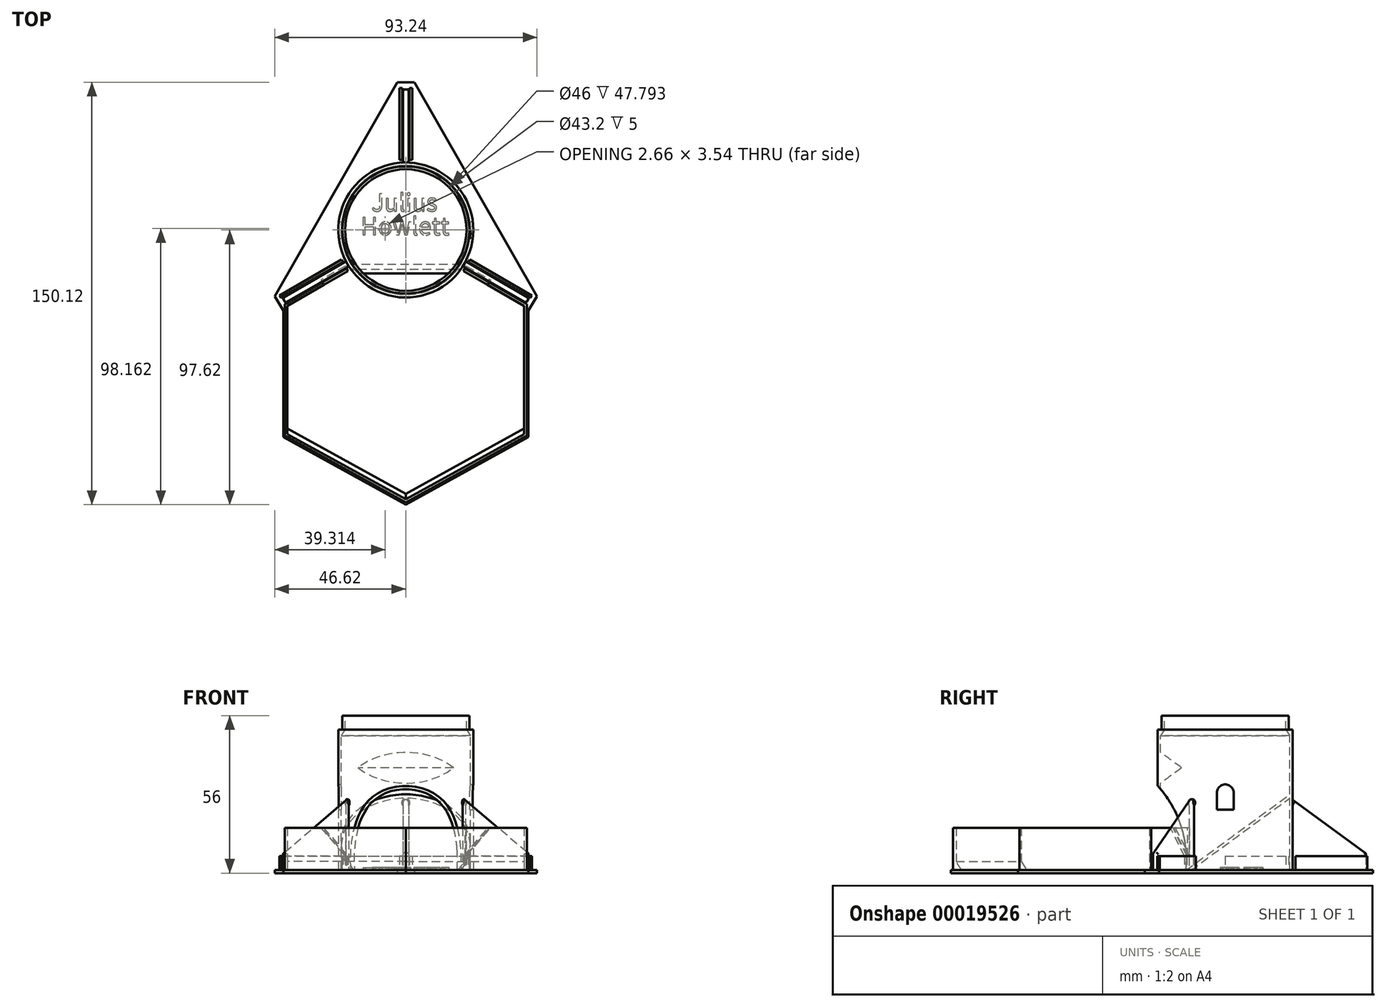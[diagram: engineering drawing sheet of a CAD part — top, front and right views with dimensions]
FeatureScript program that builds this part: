
annotation { "Feature Type Name" : "Feature", "Feature Type Description" : "" }
export const myFeature = defineFeature(function(context is Context, id is Id, definition is map)
    precondition{}
    {
        {
            var Q0;
            Q0=qCreatedBy(makeId("Top.planeOp"),FACE);
            var sketch = newSketch(context, id + "F0", { "sketchPlane" : qUnion([Q0])});
            skCircle(sketch, "E0", {"center": v(0, 0) * mm, "radius": 24 * mm});
            skSolve(sketch);
        }
        {
            var Q0;
            Q0=makeQuery(id+"F0.imprint","IMPRINT",FACE,{"disambiguationData":[TD([[makeQuery(id+"F0.imprint","IMPRINT",EDGE,{"derivedFrom":sQuery(id+"F0.wireOp",EDGE,"E0")}),1.0]])]});
            extrude(context, id + "F1", {"entities" : qUnion([Q0]), "depth" : 50 * mm});
        }
        {
            var Q0;
            Q0=makeQuery(id+"F1.opExtrude","CAP_FACE",FACE,{"disambiguationData":[OSD([sQuery(id+"F0.wireOp",EDGE,"E0")])],"isStart":false});
            var sketch = newSketch(context, id + "F2", { "sketchPlane" : qUnion([Q0])});
            skCircle(sketch, "E1", {"center": v(0, 0) * mm, "radius": 23 * mm});
            skSolve(sketch);
        }
        {
            var Q0;
            Q0=qSketchRegion(id+"F2",true);
            extrude(context, id + "F3", {"entities" : qUnion([Q0]), "operationType" : NewBodyOperationType.REMOVE, "endBound" : BoundingType.THROUGH_ALL, "oppositeDirection" : true, "depth" : 25 * mm});
        }
        {
            var Q0;
            Q0=qCreatedBy(makeId("Front.planeOp"),FACE);
            var sketch = newSketch(context, id + "F4", { "sketchPlane" : qUnion([Q0])});
            skLineSegment(sketch, "E2", {"start": v(0, 0) * mm, "end": v(0, 50) * mm});
            skLineSegment(sketch, "E3.0", {"start": v(-23.5, 50) * mm, "end": v(-23.5, 47) * mm});
            skLineSegment(sketch, "E4", {"start": v(-23.5, 50) * mm, "end": v(-22.6, 50) * mm});
            skLineSegment(sketch, "E5", {"start": v(-22.6, 50) * mm, "end": v(-22.6, 55) * mm});
            skLineSegment(sketch, "E6", {"start": v(-22.6, 55) * mm, "end": v(-21.6, 55) * mm});
            skLineSegment(sketch, "E7", {"start": v(-21.6, 55) * mm, "end": v(-21.6, 50) * mm});
            skLineSegment(sketch, "E8", {"start": v(-21.6, 50) * mm, "end": v(-23.5, 47) * mm});
            skLineSegment(sketch, "E9", {"start": v(-24, 50) * mm, "end": v(-23.5, 50) * mm});
            skSolve(sketch);
        }
        {
            var Q0;
            Q0=qSketchRegion(id+"F4",true);
            var Q1;
            Q1=makeQuery(id+"F3.boolean.opBoolean","COPY",FACE,{"derivedFrom":makeQuery(id+"F3.opExtrude","SWEPT_FACE",FACE,{"disambiguationData":[OSD([sQuery(id+"F2.wireOp",EDGE,"E1")])]})});
            revolve(context, id + "F5", {"operationType" : NewBodyOperationType.ADD, "entities" : qUnion([Q0]), "axis" : qUnion([Q1]), "revolveType" : RevolveType.FULL});
        }
        {
            var Q0;
            Q0=qCreatedBy(makeId("Top.planeOp"),FACE);
            var sketch = newSketch(context, id + "F6", { "sketchPlane" : qUnion([Q0])});
            skLineSegment(sketch, "E10", {"start": v(-1, 50) * mm, "end": v(-1, 23.5) * mm});
            skLineSegment(sketch, "E11", {"start": v(-1, 23.5) * mm, "end": v(1, 23.5) * mm});
            skLineSegment(sketch, "E12", {"start": v(1, 23.5) * mm, "end": v(1, 50) * mm});
            skLineSegment(sketch, "E13", {"start": v(-1, 50) * mm, "end": v(1, 50) * mm});
            skLineSegment(sketch, "E14.1.4", {"start": v(-20.85, -10.88) * mm, "end": v(-43.8, -24.13) * mm});
            skLineSegment(sketch, "E14.1.6", {"start": v(-42.8, -25.87) * mm, "end": v(-19.85, -12.62) * mm});
            skLineSegment(sketch, "E14.1.8", {"start": v(-19.85, -12.62) * mm, "end": v(-20.85, -10.88) * mm});
            skLineSegment(sketch, "E14.1.11", {"start": v(-42.8, -25.87) * mm, "end": v(-43.8, -24.13) * mm});
            skLineSegment(sketch, "E14.2.4", {"start": v(19.85, -12.62) * mm, "end": v(42.8, -25.87) * mm});
            skLineSegment(sketch, "E14.2.6", {"start": v(43.8, -24.13) * mm, "end": v(20.85, -10.88) * mm});
            skLineSegment(sketch, "E14.2.8", {"start": v(20.85, -10.88) * mm, "end": v(19.85, -12.62) * mm});
            skLineSegment(sketch, "E14.2.11", {"start": v(43.8, -24.13) * mm, "end": v(42.8, -25.87) * mm});
            skPoint(sketch, "E14.center", {"position": v(0, 0) * mm});
            skLineSegment(sketch, "E15", {"start": v(0, 0) * mm, "end": v(-23, 0) * mm});
            skSolve(sketch);
        }
        {
            var Q0;
            Q0=qSketchRegion(id+"F6",true);
            extrude(context, id + "F7", {"entities" : qUnion([Q0]), "operationType" : NewBodyOperationType.ADD, "depth" : 25 * mm});
        }
        {
            var Q0;
            Q0=makeQuery(id+"F7.opExtrude","SWEPT_FACE",FACE,{"disambiguationData":[OSD([sQuery(id+"F6.wireOp",EDGE,"E14.1.6")])]});
            var sketch = newSketch(context, id + "F8", { "sketchPlane" : qUnion([Q0])});
            skLineSegment(sketch, "E16", {"start": v(-23.98, 25) * mm, "end": v(-50, 25) * mm});
            skLineSegment(sketch, "E17", {"start": v(-50, 25) * mm, "end": v(-50, 6) * mm});
            skLineSegment(sketch, "E18", {"start": v(-50, 6) * mm, "end": v(-23.98, 25) * mm});
            skSolve(sketch);
        }
        {
            var Q0;
            Q0=qSketchRegion(id+"F8",true);
            extrude(context, id + "F9", {"entities" : qUnion([Q0]), "operationType" : NewBodyOperationType.REMOVE, "oppositeDirection" : true, "depth" : 2 * mm});
        }
        {
            var Q0;
            Q0=makeQuery(id+"F7.opExtrude","SWEPT_FACE",FACE,{"disambiguationData":[OSD([sQuery(id+"F6.wireOp",EDGE,"E14.2.6")])]});
            var sketch = newSketch(context, id + "F10", { "sketchPlane" : qUnion([Q0])});
            skLineSegment(sketch, "E19", {"start": v(-23.98, 25) * mm, "end": v(-50, 25) * mm});
            skLineSegment(sketch, "E20", {"start": v(-50, 25) * mm, "end": v(-50, 6) * mm});
            skLineSegment(sketch, "E21", {"start": v(-50, 6) * mm, "end": v(-23.98, 25) * mm});
            skSolve(sketch);
        }
        {
            var Q0;
            Q0=qSketchRegion(id+"F10",true);
            extrude(context, id + "F11", {"entities" : qUnion([Q0]), "operationType" : NewBodyOperationType.REMOVE, "oppositeDirection" : true, "depth" : 2 * mm});
        }
        {
            var Q0;
            Q0=makeQuery(id+"F7.opExtrude","SWEPT_FACE",FACE,{"disambiguationData":[OSD([sQuery(id+"F6.wireOp",EDGE,"E10")])]});
            var sketch = newSketch(context, id + "F12", { "sketchPlane" : qUnion([Q0])});
            skLineSegment(sketch, "E22", {"start": v(-23.98, 25) * mm, "end": v(-50, 25) * mm});
            skLineSegment(sketch, "E23", {"start": v(-50, 25) * mm, "end": v(-50, 6) * mm});
            skLineSegment(sketch, "E24", {"start": v(-23.98, 25) * mm, "end": v(-50, 6) * mm});
            skSolve(sketch);
        }
        {
            var Q0;
            Q0=qSketchRegion(id+"F12",true);
            extrude(context, id + "F13", {"entities" : qUnion([Q0]), "operationType" : NewBodyOperationType.REMOVE, "oppositeDirection" : true, "depth" : 2 * mm});
        }
        {
            var Q0;
            Q0=makeQuery(id+"F13.boolean.opBoolean","COPY",FACE,{"derivedFrom":makeQuery(id+"F13.opExtrude","SWEPT_FACE",FACE,{"disambiguationData":[OSD([sQuery(id+"F12.wireOp",EDGE,"E24")])]})});
            var Q1;
            Q1=makeQuery(id+"F9.boolean.opBoolean","COPY",FACE,{"derivedFrom":makeQuery(id+"F9.opExtrude","SWEPT_FACE",FACE,{"disambiguationData":[OSD([sQuery(id+"F8.wireOp",EDGE,"E18")])]})});
            var Q2;
            Q2=makeQuery(id+"F11.boolean.opBoolean","COPY",FACE,{"derivedFrom":makeQuery(id+"F11.opExtrude","SWEPT_FACE",FACE,{"disambiguationData":[OSD([sQuery(id+"F10.wireOp",EDGE,"E21")])]})});
            fillet(context, id + "F14", {"entities" : qUnion([Q0, Q1, Q2]), "radius" : .5 * mm, "allowEdgeOverflow" : false});
        }
        {
            var Q0;
            Q0=makeQuery(id+"F7.opExtrude","SWEPT_FACE",FACE,{"disambiguationData":[OSD([sQuery(id+"F6.wireOp",EDGE,"E14.1.11")])]});
            var Q1;
            Q1=makeQuery(id+"F7.opExtrude","SWEPT_FACE",FACE,{"disambiguationData":[OSD([sQuery(id+"F6.wireOp",EDGE,"E14.2.11")])]});
            var Q2;
            Q2=makeQuery(id+"F7.opExtrude","SWEPT_FACE",FACE,{"disambiguationData":[OSD([sQuery(id+"F6.wireOp",EDGE,"E13")])]});
            fillet(context, id + "F15", {"entities" : qUnion([Q0, Q1, Q2]), "radius" : .5 * mm, "tangentPropagation" : true, "allowEdgeOverflow" : false});
        }
        {
            var Q0;
            Q0=qCreatedBy(makeId("Right.planeOp"),FACE);
            var sketch = newSketch(context, id + "F16", { "sketchPlane" : qUnion([Q0])});
            skLineSegment(sketch, "E25", {"start": v(-24, 0) * mm, "end": v(-24, 30) * mm});
            skArc(sketch, "E26", {"start": v(-14, 0) * mm, "mid": v(-15.84, 16.05) * mm, "end": v(-24, 30) * mm});
            skLineSegment(sketch, "E27", {"start": v(-24, 0) * mm, "end": v(-14, 0) * mm});
            skSolve(sketch);
        }
        {
            var Q0;
            Q0=qSketchRegion(id+"F16",true);
            extrude(context, id + "F17", {"entities" : qUnion([Q0]), "operationType" : NewBodyOperationType.REMOVE, "oppositeDirection" : true, "depth" : 20 * mm, "hasSecondDirection" : true, "secondDirectionOppositeDirection" : false, "secondDirectionDepth" : 20 * mm});
        }
        {
            var Q0;
            Q0=qCreatedBy(makeId("Right.planeOp"),FACE);
            var sketch = newSketch(context, id + "F18", { "sketchPlane" : qUnion([Q0])});
            skCircle(sketch, "E28", {"center": v(0, 27.55) * mm, "radius": 3 * mm});
            skLineSegment(sketch, "E29.rect.bottom", {"start": v(-3, 21.55) * mm, "end": v(3, 21.55) * mm});
            skLineSegment(sketch, "E29.rect.top", {"start": v(-3, 27.55) * mm, "end": v(3, 27.55) * mm});
            skLineSegment(sketch, "E29.rect.left", {"start": v(-3, 21.55) * mm, "end": v(-3, 27.55) * mm});
            skLineSegment(sketch, "E29.rect.right", {"start": v(3, 21.55) * mm, "end": v(3, 27.55) * mm});
            skPoint(sketch, "E29.rect.middle", {"position": v(0, 24.55) * mm});
            skSolve(sketch);
        }
        {
            var Q0;
            Q0=qSketchRegion(id+"F18",true);
            extrude(context, id + "F19", {"entities" : qUnion([Q0]), "operationType" : NewBodyOperationType.REMOVE, "endBound" : BoundingType.THROUGH_ALL, "oppositeDirection" : true, "depth" : 25 * mm, "hasSecondDirection" : true, "secondDirectionBound" : SecondDirectionBoundingType.THROUGH_ALL, "secondDirectionOppositeDirection" : false, "secondDirectionDepth" : 25 * mm});
        }
        {
            var Q0;
            Q0=qCreatedBy(makeId("Right.planeOp"),FACE);
            var sketch = newSketch(context, id + "F20", { "sketchPlane" : qUnion([Q0])});
            skPoint(sketch, "E30.0", {"position": v(-14, 0) * mm});
            skLineSegment(sketch, "E31", {"start": v(-12.2, 0) * mm, "end": v(-14, 0) * mm});
            skLineSegment(sketch, "E32", {"start": v(-14, 0) * mm, "end": v(23, 27) * mm});
            skLineSegment(sketch, "E33", {"start": v(-12.2, 0) * mm, "end": v(23, 25.7) * mm});
            skLineSegment(sketch, "E34", {"start": v(23, 27) * mm, "end": v(23, 25.7) * mm});
            skLineSegment(sketch, "E35", {"start": v(-23, 30.97) * mm, "end": v(-15.49, 36.45) * mm});
            skLineSegment(sketch, "E36", {"start": v(-15.49, 36.45) * mm, "end": v(-23, 41.91) * mm});
            skLineSegment(sketch, "E37", {"start": v(-23, 41.91) * mm, "end": v(-23, 30.97) * mm});
            skSolve(sketch);
        }
        {
            var Q0;
            Q0=qSketchRegion(id+"F20",true);
            extrude(context, id + "F21", {"entities" : qUnion([Q0]), "operationType" : NewBodyOperationType.ADD, "endBound" : BoundingType.UP_TO_NEXT, "depth" : 25 * mm, "hasSecondDirection" : true, "secondDirectionBound" : SecondDirectionBoundingType.UP_TO_NEXT, "secondDirectionOppositeDirection" : true, "secondDirectionDepth" : 25 * mm});
        }
        {
            var Q0;
            Q0=qCreatedBy(makeId("Right.planeOp"),FACE);
            var sketch = newSketch(context, id + "F22", { "sketchPlane" : qUnion([Q0])});
            skLineSegment(sketch, "E38", {"start": v(0, 0) * mm, "end": v(22.6, 0) * mm});
            skLineSegment(sketch, "E39", {"start": v(22.6, 0) * mm, "end": v(22.6, 5) * mm});
            skLineSegment(sketch, "E40", {"start": v(22.6, 5) * mm, "end": v(21.6, 5) * mm});
            skLineSegment(sketch, "E41", {"start": v(21.6, 5) * mm, "end": v(21.6, 0) * mm});
            skLineSegment(sketch, "E42", {"start": v(0, 0) * mm, "end": v(0, 8.05) * mm});
            skLineSegment(sketch, "E43", {"start": v(22.6, 0) * mm, "end": v(24.4, 0) * mm});
            skLineSegment(sketch, "E44", {"start": v(24.4, 5) * mm, "end": v(25.4, 5) * mm});
            skLineSegment(sketch, "E45", {"start": v(25.4, 5) * mm, "end": v(25.4, 0) * mm});
            skLineSegment(sketch, "E46", {"start": v(25.4, 0) * mm, "end": v(24.4, 0) * mm});
            skSolve(sketch);
        }
        {
            var Q0;
            Q0 = qSketchRegion(id + "F22", true);
            var Q1;
            Q1=sQuery(id+"F22.wireOp",EDGE,"E42");
            revolve(context, id + "F23", {"operationType" : NewBodyOperationType.ADD, "entities" : qUnion([Q0]), "axis" : qUnion([Q1]), "revolveType" : RevolveType.SYMMETRIC, "angle" : 180 * degree});
        }
        {
            var Q0;
            Q0=qCreatedBy(makeId("Top.planeOp"),FACE);
            var sketch = newSketch(context, id + "F24", { "sketchPlane" : qUnion([Q0])});
            skText(sketch, "E47", { "text": "  Julius\nHowlett", "fontName": "NotoSansCJKjp-Regular.otf"});
            const initialGuessF24  = {"E47": [-0.01603, 0.0067, 1, 0, 0.00609]};
            skSetInitialGuess(sketch, initialGuessF24);
            skSolve(sketch);
        }
        {
            var Q0;
            Q0 = qSketchRegion(id + "F24", true);
            extrude(context, id + "F25", {"entities" : qUnion([Q0]), "operationType" : NewBodyOperationType.ADD, "depth" : 1 * mm});
        }
        {
            var Q0;
            Q0=qCreatedBy(makeId("Top.planeOp"),FACE);
            var sketch = newSketch(context, id + "F26", { "sketchPlane" : qUnion([Q0])});
            skLineSegment(sketch, "E48.MirrorCS", {"start": v(1.3, 50.5) * mm, "end": v(1.3, 25) * mm});
            skLineSegment(sketch, "E49.MirrorCS", {"start": v(1.3, 25) * mm, "end": v(2.3, 25) * mm});
            skPoint(sketch, "E50.center", {"position": v(0, 0) * mm});
            skLineSegment(sketch, "E51", {"start": v(2.3, 25) * mm, "end": v(2.3, 50.5) * mm});
            skLineSegment(sketch, "E52", {"start": v(1.3, 50.5) * mm, "end": v(2.3, 50.5) * mm});
            skLineSegment(sketch, "E53", {"start": v(0, 25) * mm, "end": v(0, 0) * mm});
            skLineSegment(sketch, "E54.MirrorCS", {"start": v(-1.3, 50.5) * mm, "end": v(-1.3, 25) * mm});
            skLineSegment(sketch, "E55.MirrorCS", {"start": v(-1.3, 25) * mm, "end": v(-2.3, 25) * mm});
            skLineSegment(sketch, "E56.MirrorCS", {"start": v(-2.3, 25) * mm, "end": v(-2.3, 50.5) * mm});
            skLineSegment(sketch, "E57.MirrorCS", {"start": v(-1.3, 50.5) * mm, "end": v(-2.3, 50.5) * mm});
            skLineSegment(sketch, "E58.1.0", {"start": v(-43.08, -26.38) * mm, "end": v(-21, -13.63) * mm});
            skLineSegment(sketch, "E58.1.1", {"start": v(-44.38, -24.12) * mm, "end": v(-22.3, -11.37) * mm});
            skLineSegment(sketch, "E58.1.2", {"start": v(-22.8, -10.5) * mm, "end": v(-44.88, -23.26) * mm});
            skLineSegment(sketch, "E58.1.3", {"start": v(-20.5, -14.5) * mm, "end": v(-42.58, -27.24) * mm});
            skLineSegment(sketch, "E58.1.4", {"start": v(-21, -13.63) * mm, "end": v(-20.5, -14.5) * mm});
            skLineSegment(sketch, "E58.1.5", {"start": v(-22.3, -11.37) * mm, "end": v(-22.8, -10.5) * mm});
            skLineSegment(sketch, "E58.1.6", {"start": v(-43.08, -26.38) * mm, "end": v(-42.58, -27.24) * mm});
            skLineSegment(sketch, "E58.1.7", {"start": v(-44.38, -24.12) * mm, "end": v(-44.88, -23.26) * mm});
            skLineSegment(sketch, "E58.2.0", {"start": v(44.38, -24.12) * mm, "end": v(22.3, -11.37) * mm});
            skLineSegment(sketch, "E58.2.1", {"start": v(43.08, -26.38) * mm, "end": v(21, -13.63) * mm});
            skLineSegment(sketch, "E58.2.2", {"start": v(20.5, -14.5) * mm, "end": v(42.58, -27.24) * mm});
            skLineSegment(sketch, "E58.2.3", {"start": v(22.8, -10.5) * mm, "end": v(44.88, -23.26) * mm});
            skLineSegment(sketch, "E58.2.4", {"start": v(22.3, -11.37) * mm, "end": v(22.8, -10.5) * mm});
            skLineSegment(sketch, "E58.2.5", {"start": v(21, -13.63) * mm, "end": v(20.5, -14.5) * mm});
            skLineSegment(sketch, "E58.2.6", {"start": v(44.38, -24.12) * mm, "end": v(44.88, -23.26) * mm});
            skLineSegment(sketch, "E58.2.7", {"start": v(43.08, -26.38) * mm, "end": v(42.58, -27.24) * mm});
            skSolve(sketch);
        }
        {
            var Q0;
            Q0 = qSketchRegion(id + "F26", true);
            extrude(context, id + "F27", {"entities" : qUnion([Q0]), "operationType" : NewBodyOperationType.ADD, "depth" : 5 * mm});
        }
        {
            var Q0;
            Q0=qCreatedBy(makeId("Top.planeOp"),FACE);
            var sketch = newSketch(context, id + "F28", { "sketchPlane" : qUnion([Q0])});
            skLineSegment(sketch, "E59", {"start": v(0, 52.5) * mm, "end": v(-3.04, 52.5) * mm});
            skLineSegment(sketch, "E60", {"start": v(-3.04, 52.5) * mm, "end": v(-46.62, -23.51) * mm});
            skLineSegment(sketch, "E61.MirrorCS", {"start": v(3.04, 52.5) * mm, "end": v(46.62, -23.51) * mm});
            skLineSegment(sketch, "E62.MirrorCS", {"start": v(0, 52.5) * mm, "end": v(3.04, 52.5) * mm});
            skLineSegment(sketch, "E63", {"start": v(0, 0) * mm, "end": v(0, -52.5) * mm});
            skLineSegment(sketch, "E64", {"start": v(0, 0) * mm, "end": v(0, 52.5) * mm});
            skLineSegment(sketch, "E65", {"start": v(-46.62, -23.51) * mm, "end": v(-43.55, -28.67) * mm});
            skLineSegment(sketch, "E66.MirrorCS", {"start": v(46.62, -23.51) * mm, "end": v(43.55, -28.67) * mm});
            skLineSegment(sketch, "E67", {"start": v(-43.55, -28.67) * mm, "end": v(-43.55, -73.67) * mm});
            skLineSegment(sketch, "E68.MirrorCS", {"start": v(43.55, -28.67) * mm, "end": v(43.55, -73.67) * mm});
            skLineSegment(sketch, "E69", {"start": v(-43.55, -73.67) * mm, "end": v(0, -97.62) * mm});
            skLineSegment(sketch, "E70", {"start": v(0, -97.62) * mm, "end": v(43.55, -73.67) * mm});
            skSolve(sketch);
        }
        {
            var Q0;
            Q0 = qSketchRegion(id + "F28", true);
            extrude(context, id + "F29", {"entities" : qUnion([Q0]), "depth" : .1 * mm, "hasSecondDirection" : true, "secondDirectionOppositeDirection" : true, "secondDirectionDepth" : 1 * mm});
        }
        {
            var Q0;
            Q0=makeQuery(id+"F29.opExtrude","CAP_FACE",FACE,{"disambiguationData":[OSD([sQuery(id+"F28.wireOp",EDGE,"E59"),sQuery(id+"F28.wireOp",EDGE,"E60"),sQuery(id+"F28.wireOp",EDGE,"c55cebbd-51ed-417a-9139-d7e1a8fbc767"),sQuery(id+"F28.wireOp",EDGE,"2517fbf9-24b9-4a16-a406-ebb001d36d89"),sQuery(id+"F28.wireOp",EDGE,"b6296028-9263-4a43-9658-82991aeefb18"),sQuery(id+"F28.wireOp",EDGE,"9eefc208-e5e9-4d7a-b0e8-83d086b65d660.MirrorCS"),sQuery(id+"F28.wireOp",EDGE,"e3a6379c-8aaa-4815-999c-e2b0ab7a97050.MirrorCS"),sQuery(id+"F28.wireOp",EDGE,"34469dab-9091-40de-b46f-d139c8e73abb0.MirrorCS"),sQuery(id+"F28.wireOp",EDGE,"E61.MirrorCS"),sQuery(id+"F28.wireOp",EDGE,"E62.MirrorCS")])],"isStart":false});
            var sketch = newSketch(context, id + "F30", { "sketchPlane" : qUnion([Q0])});
            skSolve(sketch);
        }
        {
            var Q0;
            Q0=makeQuery(id+"F30.imprint","IMPRINT",FACE,{"disambiguationData":[TD([[makeQuery(id+"F30.imprint","IMPRINT",EDGE,{"derivedFrom":makeQuery(id+"F29.opExtrude","CAP_EDGE",EDGE,{"disambiguationData":[OSD([sQuery(id+"F28.wireOp",EDGE,"E60")])],"isStart":false})}),1.0]])]});
            var sketch = newSketch(context, id + "F31", { "sketchPlane" : qUnion([Q0])});
            skPoint(sketch, "E71.0", {"position": v(-21, -13.63) * mm});
            skPoint(sketch, "E72.0", {"position": v(-43.08, -26.38) * mm});
            skPoint(sketch, "E73.0", {"position": v(-20.5, -14.5) * mm});
            skLineSegment(sketch, "E74", {"start": v(-20.5, -14.5) * mm, "end": v(-21, -13.63) * mm});
            skLineSegment(sketch, "E75", {"start": v(-21, -13.63) * mm, "end": v(-43.08, -26.38) * mm});
            skLineSegment(sketch, "E76", {"start": v(-43.08, -26.38) * mm, "end": v(-43.08, -73.16) * mm});
            skPoint(sketch, "E77.0", {"position": v(-43.55, -73.67) * mm});
            skPoint(sketch, "E78.0", {"position": v(0, -97.62) * mm});
            skLineSegment(sketch, "E79", {"start": v(-43.55, -73.67) * mm, "end": v(0, -97.62) * mm});
            skLineSegment(sketch, "E80", {"start": v(-43.08, -73.16) * mm, "end": v(0, -96.86) * mm});
            skLineSegment(sketch, "E81", {"start": v(-20.5, -14.5) * mm, "end": v(-42.08, -26.95) * mm});
            skLineSegment(sketch, "E82", {"start": v(-42.08, -26.95) * mm, "end": v(-42.08, -72.56) * mm});
            skLineSegment(sketch, "E83", {"start": v(-42.08, -72.56) * mm, "end": v(0, -95.71) * mm});
            skLineSegment(sketch, "E84", {"start": v(0, 0) * mm, "end": v(0, -26.88) * mm});
            skLineSegment(sketch, "E85.MirrorCS", {"start": v(20.5, -14.5) * mm, "end": v(21, -13.63) * mm});
            skLineSegment(sketch, "E86.MirrorCS", {"start": v(20.5, -14.5) * mm, "end": v(42.08, -26.95) * mm});
            skLineSegment(sketch, "E87.MirrorCS", {"start": v(21, -13.63) * mm, "end": v(43.08, -26.38) * mm});
            skLineSegment(sketch, "E88.MirrorCS", {"start": v(43.08, -26.38) * mm, "end": v(43.08, -73.16) * mm});
            skLineSegment(sketch, "E89.MirrorCS", {"start": v(42.08, -26.95) * mm, "end": v(42.08, -72.56) * mm});
            skLineSegment(sketch, "E90.MirrorCS", {"start": v(42.08, -72.56) * mm, "end": v(0, -95.71) * mm});
            skLineSegment(sketch, "E91.MirrorCS", {"start": v(43.08, -73.16) * mm, "end": v(0, -96.86) * mm});
            skSolve(sketch);
        }
        {
            var Q0;
            Q0 = qSketchRegion(id + "F31", true);
            extrude(context, id + "F32", {"entities" : qUnion([Q0]), "operationType" : NewBodyOperationType.ADD, "depth" : 15 * mm});
        }
        {
            var Q0;
            Q0=makeQuery(id+"F32.opExtrude","SWEPT_FACE",FACE,{"disambiguationData":[OSD([sQuery(id+"F31.wireOp",EDGE,"E81")])]});
            var sketch = newSketch(context, id + "F33", { "sketchPlane" : qUnion([Q0])});
            skPoint(sketch, "E92.0", {"position": v(-25, 5) * mm});
            skLineSegment(sketch, "E93", {"start": v(-25, 5) * mm, "end": v(-25, 15.1) * mm});
            skLineSegment(sketch, "E94", {"start": v(-25, 15.1) * mm, "end": v(-35, 15.1) * mm});
            skLineSegment(sketch, "E95", {"start": v(-35, 15.1) * mm, "end": v(-25, 5) * mm});
            skSolve(sketch);
        }
        {
            var Q0;
            Q0 = qSketchRegion(id + "F33", true);
            extrude(context, id + "F34", {"entities" : qUnion([Q0]), "operationType" : NewBodyOperationType.REMOVE, "oppositeDirection" : true, "depth" : 2 * mm});
        }
        {
            var Q0;
            Q0=makeQuery(id+"F32.opExtrude","SWEPT_FACE",FACE,{"disambiguationData":[OSD([sQuery(id+"F31.wireOp",EDGE,"E86.MirrorCS")])]});
            var sketch = newSketch(context, id + "F35", { "sketchPlane" : qUnion([Q0])});
            skLineSegment(sketch, "E96", {"start": v(25, 5) * mm, "end": v(25, 15.1) * mm});
            skLineSegment(sketch, "E97", {"start": v(25, 15.1) * mm, "end": v(35, 15.1) * mm});
            skLineSegment(sketch, "E98", {"start": v(25, 5) * mm, "end": v(35, 15.1) * mm});
            skSolve(sketch);
        }
        {
            var Q0;
            Q0 = qSketchRegion(id + "F35", true);
            extrude(context, id + "F36", {"entities" : qUnion([Q0]), "operationType" : NewBodyOperationType.REMOVE, "oppositeDirection" : true, "depth" : 2 * mm});
        }
        {
            var Q0;
            Q0=makeQuery(id+"F32.opExtrude","SWEPT_FACE",FACE,{"disambiguationData":[OSD([sQuery(id+"F31.wireOp",EDGE,"E82")])]});
            var sketch = newSketch(context, id + "F37", { "sketchPlane" : qUnion([Q0])});
            skLineSegment(sketch, "E99", {"start": v(-72.56, 0.1) * mm, "end": v(-72.56, 3.1) * mm});
            skLineSegment(sketch, "E100", {"start": v(-72.56, 3.1) * mm, "end": v(-70.56, 0.1) * mm});
            skLineSegment(sketch, "E101", {"start": v(-70.56, 0.1) * mm, "end": v(-72.56, 0.1) * mm});
            skSolve(sketch);
        }
        {
            var Q0;
            Q0=makeQuery(id+"F32.opExtrude","SWEPT_FACE",FACE,{"disambiguationData":[OSD([sQuery(id+"F31.wireOp",EDGE,"E83")])]});
            var sketch = newSketch(context, id + "F38", { "sketchPlane" : qUnion([Q0])});
            skLineSegment(sketch, "E102", {"start": v(-46.13, 0.1) * mm, "end": v(-46.13, 3.1) * mm});
            skLineSegment(sketch, "E103", {"start": v(-46.13, 3.1) * mm, "end": v(-44.13, 0.1) * mm});
            skLineSegment(sketch, "E104", {"start": v(-44.13, 0.1) * mm, "end": v(-46.13, 0.1) * mm});
            skSolve(sketch);
        }
        {
            var Q0;
            Q0=makeQuery(id+"F32.opExtrude","SWEPT_FACE",FACE,{"disambiguationData":[OSD([sQuery(id+"F31.wireOp",EDGE,"E90.MirrorCS")])]});
            var sketch = newSketch(context, id + "F39", { "sketchPlane" : qUnion([Q0])});
            skLineSegment(sketch, "E105", {"start": v(46.13, 0.1) * mm, "end": v(46.13, 3.1) * mm});
            skLineSegment(sketch, "E106", {"start": v(46.13, 3.1) * mm, "end": v(44.13, 0.1) * mm});
            skLineSegment(sketch, "E107", {"start": v(44.13, 0.1) * mm, "end": v(46.13, 0.1) * mm});
            skSolve(sketch);
        }
        {
            var Q0;
            Q0=makeQuery(id+"F32.opExtrude","SWEPT_FACE",FACE,{"disambiguationData":[OSD([sQuery(id+"F31.wireOp",EDGE,"E89.MirrorCS")])]});
            var sketch = newSketch(context, id + "F40", { "sketchPlane" : qUnion([Q0])});
            skLineSegment(sketch, "E108", {"start": v(72.56, 0.1) * mm, "end": v(72.56, 3.1) * mm});
            skLineSegment(sketch, "E109", {"start": v(72.56, 3.1) * mm, "end": v(70.56, 0.1) * mm});
            skLineSegment(sketch, "E110", {"start": v(70.56, 0.1) * mm, "end": v(72.56, 0.1) * mm});
            skSolve(sketch);
        }
        {
            var Q1;
            Q1=makeQuery(id+"F39.imprint","IMPRINT",FACE,{"disambiguationData":[TD([[makeQuery(id+"F39.imprint","IMPRINT",EDGE,{"derivedFrom":sQuery(id+"F39.wireOp",EDGE,"E105")}),-1.0]])]});
            var Q2;
            Q2=makeQuery(id+"F37.imprint","IMPRINT",FACE,{"disambiguationData":[TD([[makeQuery(id+"F37.imprint","IMPRINT",EDGE,{"derivedFrom":sQuery(id+"F37.wireOp",EDGE,"E99")}),1.0]])]});
            loft(context, id + "F41", {"operationType" : NewBodyOperationType.ADD, "sheetProfilesArray" : [{ "sheetProfileEntities" : qUnion([Q1]) }, { "sheetProfileEntities" : qUnion([Q2]) }]});
        }
        {
            var Q1;
            Q1=makeQuery(id+"F38.imprint","IMPRINT",FACE,{"disambiguationData":[TD([[makeQuery(id+"F38.imprint","IMPRINT",EDGE,{"derivedFrom":sQuery(id+"F38.wireOp",EDGE,"E102")}),1.0]])]});
            var Q2;
            Q2=makeQuery(id+"F40.imprint","IMPRINT",FACE,{"disambiguationData":[TD([[makeQuery(id+"F40.imprint","IMPRINT",EDGE,{"derivedFrom":sQuery(id+"F40.wireOp",EDGE,"E108")}),-1.0]])]});
            loft(context, id + "F42", {"operationType" : NewBodyOperationType.ADD, "sheetProfilesArray" : [{ "sheetProfileEntities" : qUnion([Q1]) }, { "sheetProfileEntities" : qUnion([Q2]) }]});
        }
    });
